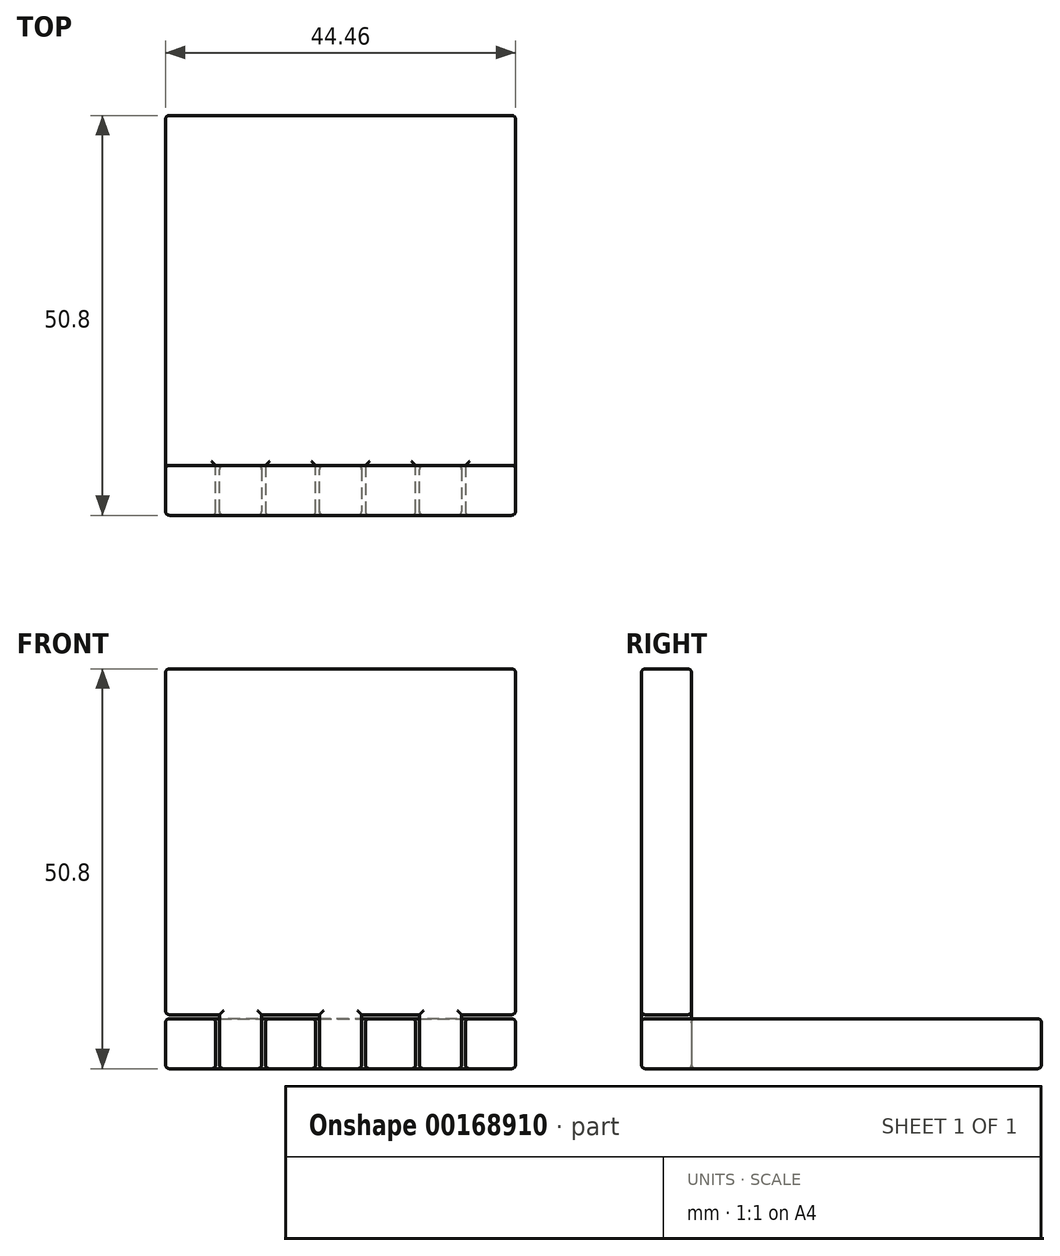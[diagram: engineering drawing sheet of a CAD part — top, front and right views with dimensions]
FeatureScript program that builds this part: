
annotation { "Feature Type Name" : "Feature", "Feature Type Description" : "" }
export const myFeature = defineFeature(function(context is Context, id is Id, definition is map)
    precondition{}
    {
        {
            var Q0;
            Q0=qCreatedBy(makeId("Top.planeOp"),FACE);
            var sketch = newSketch(context, id + "F0", { "sketchPlane" : qUnion([Q0])});
            skLineSegment(sketch, "E0.bottom", {"start": v(22.22, 25.4) * mm, "end": v(-22.23, 25.4) * mm});
            skLineSegment(sketch, "E0.top", {"start": v(22.23, -25.4) * mm, "end": v(15.88, -25.4) * mm});
            skLineSegment(sketch, "E0.left", {"start": v(22.22, 25.4) * mm, "end": v(22.23, -25.4) * mm});
            skLineSegment(sketch, "E0.right", {"start": v(-22.23, 25.4) * mm, "end": v(-22.23, -25.4) * mm});
            skPoint(sketch, "E0.middle", {"position": v(0, 0) * mm});
            skLineSegment(sketch, "E1", {"start": v(-15.88, -25.4) * mm, "end": v(-15.88, -19.05) * mm});
            skLineSegment(sketch, "E2", {"start": v(-15.88, -19.05) * mm, "end": v(-9.53, -19.05) * mm});
            skLineSegment(sketch, "E3", {"start": v(-9.53, -19.05) * mm, "end": v(-9.53, -25.4) * mm});
            skLineSegment(sketch, "E4", {"start": v(9.53, -25.4) * mm, "end": v(9.53, -19.05) * mm});
            skLineSegment(sketch, "E5", {"start": v(9.53, -19.05) * mm, "end": v(15.88, -19.05) * mm});
            skLineSegment(sketch, "E6", {"start": v(15.88, -19.05) * mm, "end": v(15.88, -25.4) * mm});
            skLineSegment(sketch, "E7", {"start": v(-3.18, -25.4) * mm, "end": v(-3.18, -19.05) * mm});
            skLineSegment(sketch, "E8", {"start": v(-3.18, -19.05) * mm, "end": v(3.17, -19.05) * mm});
            skLineSegment(sketch, "E9", {"start": v(3.17, -19.05) * mm, "end": v(3.17, -25.4) * mm});
            skLineSegment(sketch, "E10.trimOffspring", {"start": v(-15.88, -25.4) * mm, "end": v(-22.23, -25.4) * mm});
            skLineSegment(sketch, "E11.trimOffspring", {"start": v(-3.18, -25.4) * mm, "end": v(-9.53, -25.4) * mm});
            skLineSegment(sketch, "E12.trimOffspring", {"start": v(9.53, -25.4) * mm, "end": v(3.17, -25.4) * mm});
            skSolve(sketch);
        }
        {
            var Q0;
            Q0=makeQuery(id+"F0.imprint","IMPRINT",FACE,{"disambiguationData":[TD([[makeQuery(id+"F0.imprint","IMPRINT",EDGE,{"derivedFrom":sQuery(id+"F0.wireOp",EDGE,"E0.bottom")}),1.0]])]});
            extrude(context, id + "F1", {"entities" : qUnion([Q0]), "depth" : 6.35 * mm});
        }
        {
            var Q0;
            Q0=makeQuery(id+"F1.opExtrude","SWEPT_FACE",FACE,{"disambiguationData":[OSD([sQuery(id+"F0.wireOp",EDGE,"E10.trimOffspring")])]});
            var sketch = newSketch(context, id + "F2", { "sketchPlane" : qUnion([Q0])});
            skLineSegment(sketch, "E13.bottom", {"start": v(22.22, 0) * mm, "end": v(-22.23, 0) * mm});
            skLineSegment(sketch, "E13.top", {"start": v(22.22, 50.8) * mm, "end": v(-22.23, 50.8) * mm});
            skLineSegment(sketch, "E13.left", {"start": v(22.22, 0) * mm, "end": v(22.22, 50.8) * mm});
            skLineSegment(sketch, "E13.right", {"start": v(-22.23, 0) * mm, "end": v(-22.23, 50.8) * mm});
            skSolve(sketch);
        }
        {
            var Q0;
            {var subQ3=sQuery(id+"F2.wireOp",EDGE,"E13.top");Q0=makeQuery(id+"F2.imprint","IMPRINT",FACE,{"disambiguationData":[TD([[makeQuery(id+"F2.imprint","IMPRINT",EDGE,{"derivedFrom":subQ3}),1.0]])]});}
            var Q1;
            Q1=makeQuery(id+"F1.opExtrude","SWEPT_FACE",FACE,{"disambiguationData":[OSD([sQuery(id+"F0.wireOp",EDGE,"E2")])]});
            extrude(context, id + "F3", {"entities" : qUnion([Q0]), "endBound" : BoundingType.UP_TO_SURFACE, "oppositeDirection" : true, "endBoundEntityFace" : qUnion([Q1]), "depth" : 25.4 * mm});
        }
        {
            var Q0;
            Q0=makeQuery(id+"F1.opExtrude","SWEPT_BODY",BODY,{"disambiguationData":[OSD([sQuery(id+"F0.wireOp",EDGE,"E0.bottom"),sQuery(id+"F0.wireOp",EDGE,"E0.top"),sQuery(id+"F0.wireOp",EDGE,"E0.left"),sQuery(id+"F0.wireOp",EDGE,"E0.right"),sQuery(id+"F0.wireOp",EDGE,"E1"),sQuery(id+"F0.wireOp",EDGE,"E2"),sQuery(id+"F0.wireOp",EDGE,"E3"),sQuery(id+"F0.wireOp",EDGE,"E4"),sQuery(id+"F0.wireOp",EDGE,"E5"),sQuery(id+"F0.wireOp",EDGE,"E6"),sQuery(id+"F0.wireOp",EDGE,"E7"),sQuery(id+"F0.wireOp",EDGE,"E8"),sQuery(id+"F0.wireOp",EDGE,"E9"),sQuery(id+"F0.wireOp",EDGE,"E10.trimOffspring"),sQuery(id+"F0.wireOp",EDGE,"E11.trimOffspring"),sQuery(id+"F0.wireOp",EDGE,"E12.trimOffspring")])]});
            var Q1;
            Q1=makeQuery(id+"F3.opExtrude","SWEPT_BODY",BODY,{"disambiguationData":[OSD([sQuery(id+"F0.wireOp",EDGE,"E1"),sQuery(id+"F0.wireOp",EDGE,"E10.trimOffspring"),sQuery(id+"F2.wireOp",EDGE,"E13.bottom"),sQuery(id+"F2.wireOp",EDGE,"E13.top"),sQuery(id+"F2.wireOp",EDGE,"E13.left"),sQuery(id+"F2.wireOp",EDGE,"E13.right")])]});
            var Q2;
            Q2=makeQuery(id+"F1.opExtrude","CAP_FACE",FACE,{"disambiguationData":[OSD([sQuery(id+"F0.wireOp",EDGE,"E0.bottom"),sQuery(id+"F0.wireOp",EDGE,"E0.top"),sQuery(id+"F0.wireOp",EDGE,"E0.left"),sQuery(id+"F0.wireOp",EDGE,"E0.right"),sQuery(id+"F0.wireOp",EDGE,"E1"),sQuery(id+"F0.wireOp",EDGE,"E2"),sQuery(id+"F0.wireOp",EDGE,"E3"),sQuery(id+"F0.wireOp",EDGE,"E4"),sQuery(id+"F0.wireOp",EDGE,"E5"),sQuery(id+"F0.wireOp",EDGE,"E6"),sQuery(id+"F0.wireOp",EDGE,"E7"),sQuery(id+"F0.wireOp",EDGE,"E8"),sQuery(id+"F0.wireOp",EDGE,"E9"),sQuery(id+"F0.wireOp",EDGE,"E10.trimOffspring"),sQuery(id+"F0.wireOp",EDGE,"E11.trimOffspring"),sQuery(id+"F0.wireOp",EDGE,"E12.trimOffspring")])],"isStart":false});
            var Q3;
            Q3=makeQuery(id+"F3.opExtrude","CAP_FACE",FACE,{"disambiguationData":[OSD([sQuery(id+"F0.wireOp",EDGE,"E1"),sQuery(id+"F0.wireOp",EDGE,"E10.trimOffspring"),sQuery(id+"F2.wireOp",EDGE,"E13.bottom"),sQuery(id+"F2.wireOp",EDGE,"E13.top"),sQuery(id+"F2.wireOp",EDGE,"E13.left"),sQuery(id+"F2.wireOp",EDGE,"E13.right")])],"isStart":true});
            var Q4;
            Q4=makeQuery(id+"F1.opExtrude","SWEPT_FACE",FACE,{"disambiguationData":[OSD([sQuery(id+"F0.wireOp",EDGE,"E1")])]});
            var Q5;
            Q5=makeQuery(id+"F1.opExtrude","SWEPT_FACE",FACE,{"disambiguationData":[OSD([sQuery(id+"F0.wireOp",EDGE,"E3")])]});
            var Q6;
            Q6=makeQuery(id+"F1.opExtrude","SWEPT_FACE",FACE,{"disambiguationData":[OSD([sQuery(id+"F0.wireOp",EDGE,"E7")])]});
            var Q7;
            Q7=makeQuery(id+"F1.opExtrude","SWEPT_FACE",FACE,{"disambiguationData":[OSD([sQuery(id+"F0.wireOp",EDGE,"E9")])]});
            var Q8;
            Q8=makeQuery(id+"F1.opExtrude","SWEPT_FACE",FACE,{"disambiguationData":[OSD([sQuery(id+"F0.wireOp",EDGE,"E6")])]});
            var Q9;
            Q9=makeQuery(id+"F1.opExtrude","SWEPT_FACE",FACE,{"disambiguationData":[OSD([sQuery(id+"F0.wireOp",EDGE,"E4")])]});
            booleanBodies(context, id + "F4", {"operationType" : BooleanOperationType.SUBTRACTION, "tools" : qUnion([Q0]), "targets" : qUnion([Q1]), "offset" : true, "entitiesToOffset" : qUnion([Q2, Q3, Q4, Q5, Q6, Q7, Q8, Q9]), "offsetDistance" : 0.5 * mm, "keepTools" : true});
        }
        {
            var Q0;
            Q0=makeQuery(id+"F3.opExtrude","CAP_FACE",FACE,{"disambiguationData":[OSD([sQuery(id+"F0.wireOp",EDGE,"E1"),sQuery(id+"F0.wireOp",EDGE,"E10.trimOffspring"),sQuery(id+"F2.wireOp",EDGE,"E13.bottom"),sQuery(id+"F2.wireOp",EDGE,"E13.top"),sQuery(id+"F2.wireOp",EDGE,"E13.left"),sQuery(id+"F2.wireOp",EDGE,"E13.right")])],"isStart":true});
            var Q1;
            Q1=makeQuery(id+"F3.opExtrude","CAP_FACE",FACE,{"disambiguationData":[OSD([sQuery(id+"F0.wireOp",EDGE,"E1"),sQuery(id+"F0.wireOp",EDGE,"E10.trimOffspring"),sQuery(id+"F2.wireOp",EDGE,"E13.bottom"),sQuery(id+"F2.wireOp",EDGE,"E13.top"),sQuery(id+"F2.wireOp",EDGE,"E13.left"),sQuery(id+"F2.wireOp",EDGE,"E13.right")])],"isStart":false});
            var Q2;
            Q2=makeQuery(id+"F1.opExtrude","CAP_FACE",FACE,{"disambiguationData":[OSD([sQuery(id+"F0.wireOp",EDGE,"E0.bottom"),sQuery(id+"F0.wireOp",EDGE,"E0.top"),sQuery(id+"F0.wireOp",EDGE,"E0.left"),sQuery(id+"F0.wireOp",EDGE,"E0.right"),sQuery(id+"F0.wireOp",EDGE,"E1"),sQuery(id+"F0.wireOp",EDGE,"E2"),sQuery(id+"F0.wireOp",EDGE,"E3"),sQuery(id+"F0.wireOp",EDGE,"E4"),sQuery(id+"F0.wireOp",EDGE,"E5"),sQuery(id+"F0.wireOp",EDGE,"E6"),sQuery(id+"F0.wireOp",EDGE,"E7"),sQuery(id+"F0.wireOp",EDGE,"E8"),sQuery(id+"F0.wireOp",EDGE,"E9"),sQuery(id+"F0.wireOp",EDGE,"E10.trimOffspring"),sQuery(id+"F0.wireOp",EDGE,"E11.trimOffspring"),sQuery(id+"F0.wireOp",EDGE,"E12.trimOffspring")])],"isStart":false});
            var Q3;
            Q3=makeQuery(id+"F1.opExtrude","CAP_FACE",FACE,{"disambiguationData":[OSD([sQuery(id+"F0.wireOp",EDGE,"E0.bottom"),sQuery(id+"F0.wireOp",EDGE,"E0.top"),sQuery(id+"F0.wireOp",EDGE,"E0.left"),sQuery(id+"F0.wireOp",EDGE,"E0.right"),sQuery(id+"F0.wireOp",EDGE,"E1"),sQuery(id+"F0.wireOp",EDGE,"E2"),sQuery(id+"F0.wireOp",EDGE,"E3"),sQuery(id+"F0.wireOp",EDGE,"E4"),sQuery(id+"F0.wireOp",EDGE,"E5"),sQuery(id+"F0.wireOp",EDGE,"E6"),sQuery(id+"F0.wireOp",EDGE,"E7"),sQuery(id+"F0.wireOp",EDGE,"E8"),sQuery(id+"F0.wireOp",EDGE,"E9"),sQuery(id+"F0.wireOp",EDGE,"E10.trimOffspring"),sQuery(id+"F0.wireOp",EDGE,"E11.trimOffspring"),sQuery(id+"F0.wireOp",EDGE,"E12.trimOffspring")])],"isStart":true});
            var Q4;
            Q4=makeQuery(id+"F3.opExtrude","SWEPT_FACE",FACE,{"disambiguationData":[OSD([sQuery(id+"F2.wireOp",EDGE,"E13.right")])]});
            var Q5;
            Q5=makeQuery(id+"F3.opExtrude","SWEPT_FACE",FACE,{"disambiguationData":[OSD([sQuery(id+"F2.wireOp",EDGE,"E13.top")])]});
            var Q6;
            Q6=makeQuery(id+"F3.opExtrude","SWEPT_FACE",FACE,{"disambiguationData":[OSD([sQuery(id+"F2.wireOp",EDGE,"E13.left")])]});
            var Q7;
            Q7=makeQuery(id+"F1.opExtrude","SWEPT_FACE",FACE,{"disambiguationData":[OSD([sQuery(id+"F0.wireOp",EDGE,"E0.left")])]});
            var Q8;
            Q8=makeQuery(id+"F1.opExtrude","SWEPT_FACE",FACE,{"disambiguationData":[OSD([sQuery(id+"F0.wireOp",EDGE,"E0.bottom")])]});
            var Q9;
            Q9=makeQuery(id+"F1.opExtrude","SWEPT_FACE",FACE,{"disambiguationData":[OSD([sQuery(id+"F0.wireOp",EDGE,"E0.right")])]});
            var Q10;
            {var subQ3=sQuery(id+"F2.wireOp",EDGE,"E13.bottom");var subQ5=sQuery(id+"F0.wireOp",EDGE,"E1");Q10=makeQuery(id+"F4.tempBoolean.opBoolean","SPLIT",FACE,{"disambiguationData":[TD([makeQuery(id+"F4.offsetTempBody.opPattern","COPY",FACE,{"derivedFrom":makeQuery(id+"F1.opExtrude","SWEPT_FACE",FACE,{"disambiguationData":[OSD([subQ5])]}),"instanceName":"1"})])],"derivedFrom":makeQuery(id+"F3.opExtrude","SWEPT_FACE",FACE,{"disambiguationData":[OSD([subQ3])]})});}
            var Q11;
            {var subQ3=sQuery(id+"F2.wireOp",EDGE,"E13.bottom");Q11=makeQuery(id+"F4.tempBoolean.opBoolean","SPLIT",FACE,{"disambiguationData":[TD([makeQuery(id+"F4.offsetTempBody.opPattern","COPY",FACE,{"derivedFrom":makeQuery(id+"F1.opExtrude","SWEPT_FACE",FACE,{"disambiguationData":[OSD([sQuery(id+"F0.wireOp",EDGE,"E7")])]}),"instanceName":"1"})])],"derivedFrom":makeQuery(id+"F3.opExtrude","SWEPT_FACE",FACE,{"disambiguationData":[OSD([subQ3])]})});}
            var Q12;
            {var subQ3=sQuery(id+"F2.wireOp",EDGE,"E13.bottom");Q12=makeQuery(id+"F4.tempBoolean.opBoolean","SPLIT",FACE,{"disambiguationData":[TD([makeQuery(id+"F4.offsetTempBody.opPattern","COPY",FACE,{"derivedFrom":makeQuery(id+"F1.opExtrude","SWEPT_FACE",FACE,{"disambiguationData":[OSD([sQuery(id+"F0.wireOp",EDGE,"E4")])]}),"instanceName":"1"})])],"derivedFrom":makeQuery(id+"F3.opExtrude","SWEPT_FACE",FACE,{"disambiguationData":[OSD([subQ3])]})});}
            var Q13;
            Q13=makeQuery(id+"F1.opExtrude","SWEPT_FACE",FACE,{"disambiguationData":[OSD([sQuery(id+"F0.wireOp",EDGE,"E0.top")])]});
            var Q14;
            Q14=makeQuery(id+"F1.opExtrude","SWEPT_FACE",FACE,{"disambiguationData":[OSD([sQuery(id+"F0.wireOp",EDGE,"E12.trimOffspring")])]});
            var Q15;
            Q15=makeQuery(id+"F1.opExtrude","SWEPT_FACE",FACE,{"disambiguationData":[OSD([sQuery(id+"F0.wireOp",EDGE,"E11.trimOffspring")])]});
            var Q16;
            Q16=makeQuery(id+"F1.opExtrude","SWEPT_FACE",FACE,{"disambiguationData":[OSD([sQuery(id+"F0.wireOp",EDGE,"E10.trimOffspring")])]});
            fillet(context, id + "F5", {"entities" : qUnion([Q0, Q1, Q2, Q3, Q4, Q5, Q6, Q7, Q8, Q9, Q10, Q11, Q12, Q13, Q14, Q15, Q16]), "radius" : 0.5 * mm, "tangentPropagation" : true, "allowEdgeOverflow" : false});
        }
    });
